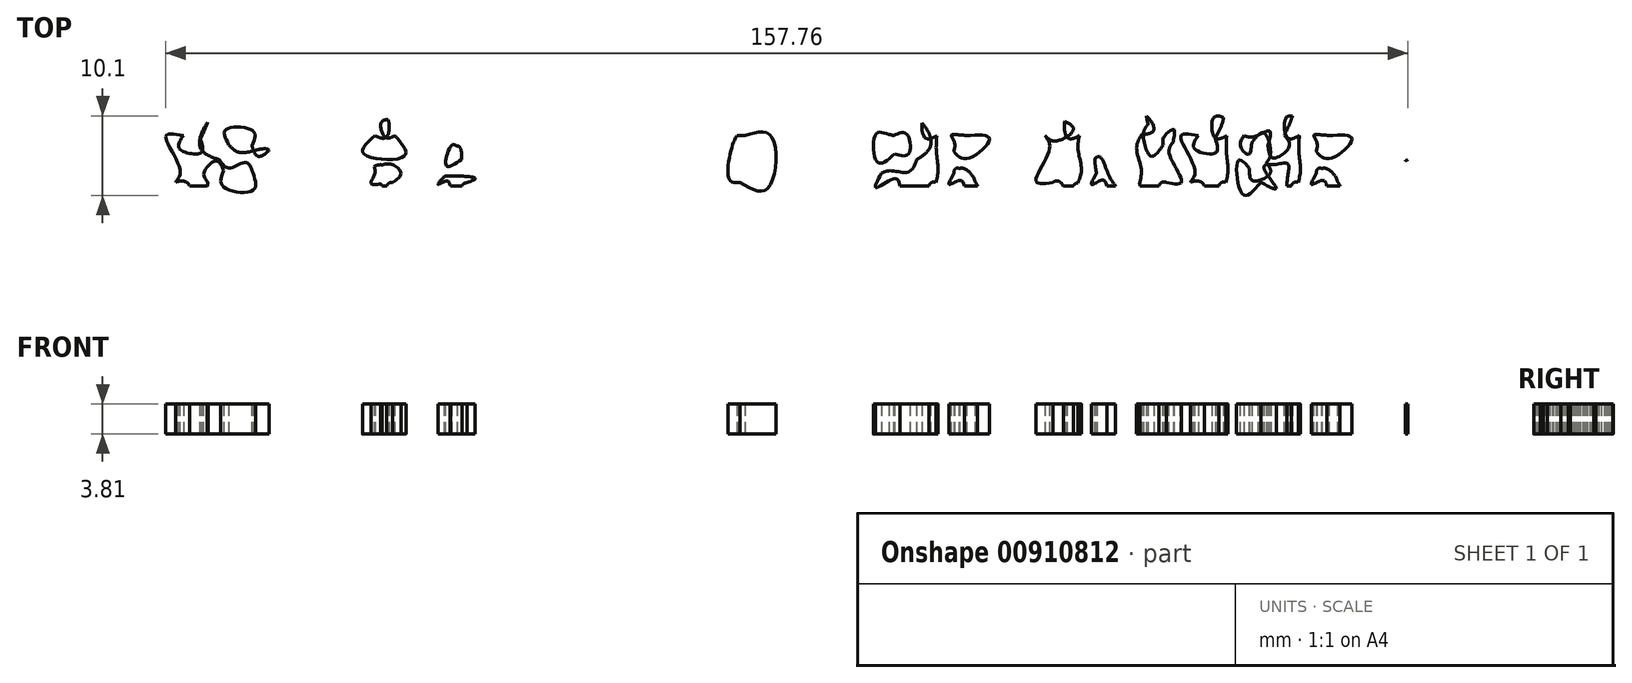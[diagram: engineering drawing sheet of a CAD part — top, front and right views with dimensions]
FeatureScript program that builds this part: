
annotation { "Feature Type Name" : "Feature", "Feature Type Description" : "" }
export const myFeature = defineFeature(function(context is Context, id is Id, definition is map)
    precondition{}
    {
        {
            var Q0;
            Q0=qCreatedBy(makeId("Top.planeOp"),FACE);
            var sketch = newSketch(context, id + "F0", { "sketchPlane" : qUnion([Q0])});
            skLineSegment(sketch, "E0", {"start": v(-392.16, 161.06) * mm, "end": v(-389.78, 161.06) * mm});
            skLineSegment(sketch, "E1", {"start": v(-389.78, 161.06) * mm, "end": v(-385.07, 161.06) * mm});
            skLineSegment(sketch, "E2", {"start": v(-383.48, 161.06) * mm, "end": v(-377.66, 161.06) * mm});
            skLineSegment(sketch, "E3", {"start": v(-374.78, 161.06) * mm, "end": v(-361.4, 161.06) * mm});
            skLineSegment(sketch, "E4", {"start": v(-360.93, 161.06) * mm, "end": v(-360.68, 161.06) * mm});
            skLineSegment(sketch, "E5", {"start": v(-358.96, 161.06) * mm, "end": v(-356.75, 161.06) * mm});
            skLineSegment(sketch, "E6", {"start": v(-356.3, 161.06) * mm, "end": v(-356.04, 161.06) * mm});
            skLineSegment(sketch, "E7", {"start": v(-354.31, 161.06) * mm, "end": v(-352.5, 161.06) * mm});
            skLineSegment(sketch, "E8", {"start": v(-350.4, 161.06) * mm, "end": v(-347.14, 161.06) * mm});
            skLineSegment(sketch, "E9", {"start": v(-346.7, 161.06) * mm, "end": v(-346.26, 161.06) * mm});
            skLineSegment(sketch, "E10", {"start": v(-344.65, 161.06) * mm, "end": v(-341.9, 161.06) * mm});
            skLineSegment(sketch, "E11", {"start": v(-339.56, 161.06) * mm, "end": v(-339.12, 161.06) * mm});
            skLineSegment(sketch, "E12", {"start": v(-336.77, 161.06) * mm, "end": v(-322.47, 161.06) * mm});
            skLineSegment(sketch, "E13", {"start": v(-319.67, 161.06) * mm, "end": v(-315.49, 161.06) * mm});
            skLineSegment(sketch, "E14", {"start": v(-315.06, 161.06) * mm, "end": v(-314.5, 161.06) * mm});
            skLineSegment(sketch, "E15", {"start": v(-311.92, 161.06) * mm, "end": v(-294.7, 161.06) * mm});
            skLineSegment(sketch, "E16", {"start": v(-293.3, 161.06) * mm, "end": v(-286.65, 161.06) * mm});
            skLineSegment(sketch, "E17", {"start": v(-285.25, 161.06) * mm, "end": v(-280.95, 161.06) * mm});
            skLineSegment(sketch, "E18", {"start": v(-280, 161.06) * mm, "end": v(-276.71, 161.06) * mm});
            skLineSegment(sketch, "E19", {"start": v(-274.31, 161.06) * mm, "end": v(-269.46, 161.06) * mm});
            skLineSegment(sketch, "E20", {"start": v(-269.04, 161.06) * mm, "end": v(-268.7, 161.06) * mm});
            skLineSegment(sketch, "E21", {"start": v(-267.03, 161.06) * mm, "end": v(-263.02, 161.06) * mm});
            skLineSegment(sketch, "E22", {"start": v(-262.74, 161.06) * mm, "end": v(-256.16, 161.06) * mm});
            skLineSegment(sketch, "E23", {"start": v(-254.57, 161.06) * mm, "end": v(-240.61, 161.06) * mm});
            skLineSegment(sketch, "E24", {"start": v(-239.21, 161.06) * mm, "end": v(-234.91, 161.06) * mm});
            skLineSegment(sketch, "E25", {"start": v(-233.97, 161.06) * mm, "end": v(-218.67, 161.06) * mm});
            skLineSegment(sketch, "E26", {"start": v(-219.23, 162.84) * mm, "end": v(-224.08, 162.84) * mm});
            skLineSegment(sketch, "E27", {"start": v(-228.3, 162.84) * mm, "end": v(-233.11, 162.84) * mm});
            skLineSegment(sketch, "E28", {"start": v(-242.59, 162.84) * mm, "end": v(-243.12, 162.84) * mm});
            skLineSegment(sketch, "E29", {"start": v(-251.8, 162.84) * mm, "end": v(-253.6, 162.84) * mm});
            skLineSegment(sketch, "E30", {"start": v(-259.4, 162.84) * mm, "end": v(-261.8, 162.84) * mm});
            skLineSegment(sketch, "E31", {"start": v(-270.25, 162.84) * mm, "end": v(-271.55, 162.84) * mm});
            skLineSegment(sketch, "E32", {"start": v(-278.26, 162.84) * mm, "end": v(-279.15, 162.84) * mm});
            skLineSegment(sketch, "E33", {"start": v(-288.63, 162.84) * mm, "end": v(-292.26, 162.84) * mm});
            skLineSegment(sketch, "E34", {"start": v(-297.83, 162.84) * mm, "end": v(-308.5, 162.84) * mm});
            skLineSegment(sketch, "E35", {"start": v(-316.27, 162.84) * mm, "end": v(-317.6, 162.84) * mm});
            skLineSegment(sketch, "E36", {"start": v(-324.8, 162.84) * mm, "end": v(-335.4, 162.84) * mm});
            skLineSegment(sketch, "E37", {"start": v(-343.18, 162.84) * mm, "end": v(-343.57, 162.84) * mm});
            skLineSegment(sketch, "E38", {"start": v(-362.15, 162.84) * mm, "end": v(-372.55, 162.84) * mm});
            skLineSegment(sketch, "E39", {"start": v(-380.27, 162.84) * mm, "end": v(-382.52, 162.84) * mm});
            skLineSegment(sketch, "E40", {"start": v(-388.3, 162.84) * mm, "end": v(-389.78, 162.84) * mm});
            skLineSegment(sketch, "E41", {"start": v(-312.98, 169.2) * mm, "end": v(-311.96, 169.2) * mm});
            skLineSegment(sketch, "E42", {"start": v(-264.94, 162.84) * mm, "end": v(-266, 162.84) * mm});
            skLineSegment(sketch, "E43", {"start": v(-357.5, 162.84) * mm, "end": v(-358.06, 162.84) * mm});
            skLineSegment(sketch, "E44", {"start": v(-282.44, 162.84) * mm, "end": v(-284.08, 162.84) * mm});
            skLineSegment(sketch, "E45", {"start": v(-236.4, 162.84) * mm, "end": v(-238.04, 162.84) * mm});
            skLineSegment(sketch, "E46", {"start": v(-347.92, 162.84) * mm, "end": v(-349.37, 162.84) * mm});
            skFitSpline(sketch, "E47", {"points": [v(-411.77, 178.81) * mm, v(-412, 178.82) * mm, v(-412.23, 178.74) * mm, v(-412.4, 178.59) * mm]});
            skFitSpline(sketch, "E48", {"points": [v(-412.4, 178.59) * mm, v(-412.4, 178.59) * mm, v(-412.4, 178.59) * mm, v(-412.41, 178.58) * mm, v(-414.56, 176.7) * mm, v(-416.6, 174.1) * mm]});
            skFitSpline(sketch, "E49", {"points": [v(-416.6, 174.1) * mm, v(-418.66, 171.49) * mm, v(-420.75, 168.13) * mm, v(-420.28, 164.84) * mm]});
            skFitSpline(sketch, "E50", {"points": [v(-420.28, 164.84) * mm, v(-419.83, 161.73) * mm, v(-417.73, 158.5) * mm, v(-415.02, 155.94) * mm]});
            skFitSpline(sketch, "E51", {"points": [v(-415.02, 155.94) * mm, v(-412.31, 153.37) * mm, v(-408.96, 151.45) * mm, v(-405.73, 151.27) * mm]});
            skFitSpline(sketch, "E52", {"points": [v(-405.73, 151.27) * mm, v(-402.3, 151.08) * mm, v(-398.95, 153.74) * mm, v(-396.34, 156.3) * mm]});
            skFitSpline(sketch, "E53", {"points": [v(-396.34, 156.3) * mm, v(-394.03, 158.55) * mm, v(-392.52, 160.56) * mm, v(-392.16, 161.06) * mm]});
            skFitSpline(sketch, "E54", {"points": [v(-385.07, 161.06) * mm, v(-384.5, 161) * mm, v(-383.96, 160.95) * mm, v(-383.48, 161.06) * mm]});
            skFitSpline(sketch, "E55", {"points": [v(-377.66, 161.06) * mm, v(-376.76, 160.72) * mm, v(-375.7, 160.74) * mm, v(-374.78, 161.06) * mm]});
            skFitSpline(sketch, "E56", {"points": [v(-361.4, 161.06) * mm, v(-361.25, 161.02) * mm, v(-361.1, 161.02) * mm, v(-360.93, 161.06) * mm]});
            skFitSpline(sketch, "E57", {"points": [v(-360.68, 161.06) * mm, v(-360.2, 160.85) * mm, v(-359.53, 160.87) * mm, v(-358.96, 161.06) * mm]});
            skFitSpline(sketch, "E58", {"points": [v(-356.75, 161.06) * mm, v(-356.61, 161.02) * mm, v(-356.46, 161.02) * mm, v(-356.3, 161.06) * mm]});
            skFitSpline(sketch, "E59", {"points": [v(-356.04, 161.06) * mm, v(-355.56, 160.85) * mm, v(-354.89, 160.87) * mm, v(-354.31, 161.06) * mm]});
            skFitSpline(sketch, "E60", {"points": [v(-352.5, 161.06) * mm, v(-351.97, 160.91) * mm, v(-351.12, 160.89) * mm, v(-350.4, 161.06) * mm]});
            skFitSpline(sketch, "E61", {"points": [v(-347.14, 161.06) * mm, v(-347, 161.03) * mm, v(-346.86, 161.02) * mm, v(-346.7, 161.06) * mm]});
            skFitSpline(sketch, "E62", {"points": [v(-346.26, 161.06) * mm, v(-345.8, 161) * mm, v(-345.2, 160.97) * mm, v(-344.65, 161.06) * mm]});
            skFitSpline(sketch, "E63", {"points": [v(-341.9, 161.06) * mm, v(-341.2, 160.9) * mm, v(-340.35, 160.93) * mm, v(-339.56, 161.06) * mm]});
            skFitSpline(sketch, "E64", {"points": [v(-339.12, 161.06) * mm, v(-338.17, 160.89) * mm, v(-337.38, 160.88) * mm, v(-336.77, 161.06) * mm]});
            skFitSpline(sketch, "E65", {"points": [v(-322.47, 161.06) * mm, v(-321.92, 160.93) * mm, v(-321.35, 160.87) * mm, v(-320.9, 160.86) * mm]});
            skFitSpline(sketch, "E66", {"points": [v(-320.9, 160.86) * mm, v(-320.48, 160.84) * mm, v(-320.06, 160.91) * mm, v(-319.67, 161.06) * mm]});
            skFitSpline(sketch, "E67", {"points": [v(-315.49, 161.06) * mm, v(-315.35, 161.03) * mm, v(-315.21, 161.03) * mm, v(-315.06, 161.06) * mm]});
            skFitSpline(sketch, "E68", {"points": [v(-314.5, 161.06) * mm, v(-313.67, 160.97) * mm, v(-312.78, 160.95) * mm, v(-311.92, 161.06) * mm]});
            skFitSpline(sketch, "E69", {"points": [v(-294.7, 161.06) * mm, v(-294.2, 161) * mm, v(-293.72, 160.98) * mm, v(-293.3, 161.06) * mm]});
            skFitSpline(sketch, "E70", {"points": [v(-286.65, 161.06) * mm, v(-286.2, 161.03) * mm, v(-285.7, 161) * mm, v(-285.25, 161.06) * mm]});
            skFitSpline(sketch, "E71", {"points": [v(-280.95, 161.06) * mm, v(-280.69, 160.96) * mm, v(-280.38, 160.95) * mm, v(-280, 161.06) * mm]});
            skFitSpline(sketch, "E72", {"points": [v(-276.71, 161.06) * mm, v(-275.93, 160.98) * mm, v(-275.12, 161) * mm, v(-274.31, 161.06) * mm]});
            skFitSpline(sketch, "E73", {"points": [v(-269.46, 161.06) * mm, v(-269.33, 161.03) * mm, v(-269.19, 161.03) * mm, v(-269.04, 161.06) * mm]});
            skFitSpline(sketch, "E74", {"points": [v(-268.7, 161.06) * mm, v(-268.25, 160.96) * mm, v(-267.6, 160.94) * mm, v(-267.03, 161.06) * mm]});
            skFitSpline(sketch, "E75", {"points": [v(-263.02, 161.06) * mm, v(-262.93, 161.05) * mm, v(-262.83, 161.05) * mm, v(-262.74, 161.06) * mm]});
            skFitSpline(sketch, "E76", {"points": [v(-256.16, 161.06) * mm, v(-255.6, 161) * mm, v(-255.05, 160.95) * mm, v(-254.57, 161.06) * mm]});
            skFitSpline(sketch, "E77", {"points": [v(-240.61, 161.06) * mm, v(-240.16, 161.03) * mm, v(-239.66, 161) * mm, v(-239.21, 161.06) * mm]});
            skFitSpline(sketch, "E78", {"points": [v(-234.91, 161.06) * mm, v(-234.65, 160.96) * mm, v(-234.34, 160.95) * mm, v(-233.97, 161.06) * mm]});
            skFitSpline(sketch, "E79", {"points": [v(-218.67, 161.06) * mm, v(-218.3, 161.05) * mm, v(-217.97, 161.28) * mm, v(-217.84, 161.63) * mm]});
            skFitSpline(sketch, "E80", {"points": [v(-217.84, 161.63) * mm, v(-217.4, 161.82) * mm, v(-217.05, 162.25) * mm, v(-217.08, 162.82) * mm]});
            skFitSpline(sketch, "E81", {"points": [v(-217.08, 162.82) * mm, v(-215.9, 167) * mm, v(-218.01, 171.83) * mm, v(-221.91, 173.63) * mm]});
            skFitSpline(sketch, "E82", {"points": [v(-221.91, 173.63) * mm, v(-222.1, 173.67) * mm, v(-222.3, 173.64) * mm, v(-222.47, 173.56) * mm]});
            skFitSpline(sketch, "E83", {"points": [v(-222.47, 173.56) * mm, v(-224.14, 172.5) * mm, v(-222, 171.05) * mm, v(-221.2, 170.27) * mm]});
            skFitSpline(sketch, "E84", {"points": [v(-221.2, 170.27) * mm, v(-219.3, 168.29) * mm, v(-218.98, 165.47) * mm, v(-219.23, 162.84) * mm]});
            skFitSpline(sketch, "E85", {"points": [v(-224.08, 162.84) * mm, v(-223.18, 164.27) * mm, v(-223.73, 166.65) * mm, v(-225.8, 166.73) * mm]});
            skFitSpline(sketch, "E86", {"points": [v(-225.8, 166.73) * mm, v(-225.9, 166.74) * mm, v(-226.01, 166.74) * mm, v(-226.11, 166.74) * mm]});
            skFitSpline(sketch, "E87", {"points": [v(-227.8, 166.15) * mm, v(-228.88, 165.4) * mm, v(-228.92, 163.9) * mm, v(-228.3, 162.84) * mm]});
            skFitSpline(sketch, "E88", {"points": [v(-233.11, 162.84) * mm, v(-233.31, 163.15) * mm, v(-233.65, 163.36) * mm, v(-234.1, 163.28) * mm]});
            skFitSpline(sketch, "E89", {"points": [v(-234.1, 163.28) * mm, v(-234.42, 164.16) * mm, v(-235.54, 165.19) * mm, v(-235.61, 165.85) * mm]});
            skFitSpline(sketch, "E90", {"points": [v(-235.61, 165.85) * mm, v(-233.22, 167.2) * mm, v(-234.4, 170.84) * mm, v(-236.83, 171.27) * mm]});
            skFitSpline(sketch, "E91", {"points": [v(-236.83, 171.27) * mm, v(-238.4, 171.6) * mm, v(-240.06, 171.3) * mm, v(-241.66, 171.4) * mm]});
            skFitSpline(sketch, "E92", {"points": [v(-241.66, 171.4) * mm, v(-243.21, 171.52) * mm, v(-243.08, 168.97) * mm, v(-241.56, 169.2) * mm]});
            skFitSpline(sketch, "E93", {"points": [v(-241.56, 169.2) * mm, v(-241.63, 167.27) * mm, v(-241.42, 165.05) * mm, v(-241.66, 163.28) * mm]});
            skFitSpline(sketch, "E94", {"points": [v(-241.66, 163.28) * mm, v(-242.1, 163.32) * mm, v(-242.41, 163.13) * mm, v(-242.59, 162.84) * mm]});
            skFitSpline(sketch, "E95", {"points": [v(-243.12, 162.84) * mm, v(-243.02, 164.19) * mm, v(-243, 165.62) * mm, v(-244.52, 165.51) * mm]});
            skFitSpline(sketch, "E96", {"points": [v(-244.52, 165.51) * mm, v(-246.05, 165.2) * mm, v(-244.5, 162.54) * mm, v(-246.47, 163.28) * mm]});
            skFitSpline(sketch, "E97", {"points": [v(-246.47, 163.28) * mm, v(-248.75, 161.76) * mm, v(-249.32, 166.02) * mm, v(-247.87, 165.01) * mm]});
            skFitSpline(sketch, "E98", {"points": [v(-247.87, 165.01) * mm, v(-247.47, 163.5) * mm, v(-245.28, 164.38) * mm, v(-245.75, 165.79) * mm]});
            skFitSpline(sketch, "E99", {"points": [v(-245.75, 165.79) * mm, v(-245.2, 166.97) * mm, v(-246.08, 169.56) * mm, v(-247.6, 168.3) * mm]});
            skFitSpline(sketch, "E100", {"points": [v(-247.6, 168.3) * mm, v(-248.03, 166.83) * mm, v(-249.02, 167.86) * mm, v(-248.6, 169.2) * mm]});
            skFitSpline(sketch, "E101", {"points": [v(-248.6, 169.2) * mm, v(-247.22, 169.1) * mm, v(-245.35, 169.8) * mm, v(-245.55, 167.96) * mm]});
            skFitSpline(sketch, "E102", {"points": [v(-245.55, 167.96) * mm, v(-244.86, 166.37) * mm, v(-242.84, 167.85) * mm, v(-243.47, 169.24) * mm]});
            skFitSpline(sketch, "E103", {"points": [v(-243.47, 169.24) * mm, v(-242.5, 172.63) * mm, v(-246.43, 171.06) * mm, v(-248.46, 171.4) * mm]});
            skFitSpline(sketch, "E104", {"points": [v(-248.46, 171.4) * mm, v(-249.27, 171.4) * mm, v(-250.07, 171.4) * mm, v(-250.87, 171.4) * mm]});
            skFitSpline(sketch, "E105", {"points": [v(-250.87, 171.4) * mm, v(-252.42, 171.52) * mm, v(-252.29, 168.97) * mm, v(-250.77, 169.2) * mm]});
            skFitSpline(sketch, "E106", {"points": [v(-250.77, 169.2) * mm, v(-250.84, 167.27) * mm, v(-250.63, 165.05) * mm, v(-250.86, 163.28) * mm]});
            skFitSpline(sketch, "E107", {"points": [v(-250.86, 163.28) * mm, v(-251.31, 163.32) * mm, v(-251.62, 163.13) * mm, v(-251.8, 162.84) * mm]});
            skFitSpline(sketch, "E108", {"points": [v(-253.6, 162.84) * mm, v(-254, 163.3) * mm, v(-254.83, 163.43) * mm, v(-255.41, 163.28) * mm]});
            skFitSpline(sketch, "E109", {"points": [v(-255.41, 163.28) * mm, v(-254.85, 165.03) * mm, v(-256.62, 169.14) * mm, v(-254.4, 169.2) * mm]});
            skFitSpline(sketch, "E110", {"points": [v(-254.4, 169.2) * mm, v(-254.89, 167.58) * mm, v(-252.19, 167.03) * mm, v(-252.24, 168.8) * mm]});
            skFitSpline(sketch, "E111", {"points": [v(-252.24, 168.8) * mm, v(-251.32, 171.9) * mm, v(-253.82, 171.53) * mm, v(-256.07, 171.4) * mm]});
            skFitSpline(sketch, "E112", {"points": [v(-256.07, 171.4) * mm, v(-257.39, 171) * mm, v(-260.75, 172.27) * mm, v(-260.77, 170.62) * mm]});
            skFitSpline(sketch, "E113", {"points": [v(-260.77, 170.62) * mm, v(-261.37, 169.39) * mm, v(-260.4, 166.61) * mm, v(-258.85, 168.05) * mm]});
            skFitSpline(sketch, "E114", {"points": [v(-258.85, 168.05) * mm, v(-258.75, 169.07) * mm, v(-257.54, 169.97) * mm, v(-257.58, 168.43) * mm]});
            skFitSpline(sketch, "E115", {"points": [v(-257.58, 168.43) * mm, v(-258.08, 166.92) * mm, v(-256.52, 163.33) * mm, v(-258.46, 163.28) * mm]});
            skFitSpline(sketch, "E116", {"points": [v(-258.46, 163.28) * mm, v(-258.9, 163.32) * mm, v(-259.21, 163.13) * mm, v(-259.4, 162.84) * mm]});
            skFitSpline(sketch, "E117", {"points": [v(-261.8, 162.84) * mm, v(-261.82, 162.9) * mm, v(-261.84, 162.97) * mm, v(-261.86, 163.03) * mm]});
            skFitSpline(sketch, "E118", {"points": [v(-261.86, 163.03) * mm, v(-261.66, 165.04) * mm, v(-262.24, 167.64) * mm, v(-261.6, 169.3) * mm]});
            skFitSpline(sketch, "E119", {"points": [v(-261.6, 169.3) * mm, v(-260.04, 170.02) * mm, v(-261.5, 172.03) * mm, v(-262.87, 171.4) * mm]});
            skFitSpline(sketch, "E120", {"points": [v(-262.87, 171.4) * mm, v(-264.14, 172.1) * mm, v(-266.66, 170.74) * mm, v(-265.1, 169.4) * mm]});
            skFitSpline(sketch, "E121", {"points": [v(-265.1, 169.4) * mm, v(-263.7, 169.28) * mm, v(-264, 168.17) * mm, v(-264.02, 166.87) * mm]});
            skFitSpline(sketch, "E122", {"points": [v(-264.02, 166.87) * mm, v(-263.87, 163.95) * mm, v(-266.1, 169.65) * mm, v(-267, 170.56) * mm]});
            skFitSpline(sketch, "E123", {"points": [v(-267, 170.56) * mm, v(-267.36, 171.93) * mm, v(-268.58, 171.23) * mm, v(-269.6, 171.4) * mm]});
            skFitSpline(sketch, "E124", {"points": [v(-269.6, 171.4) * mm, v(-271.16, 171.52) * mm, v(-271.03, 168.97) * mm, v(-269.5, 169.2) * mm]});
            skFitSpline(sketch, "E125", {"points": [v(-269.5, 169.2) * mm, v(-269.65, 167.28) * mm, v(-269.24, 164.9) * mm, v(-269.69, 163.22) * mm]});
            skFitSpline(sketch, "E126", {"points": [v(-269.69, 163.22) * mm, v(-269.95, 163.14) * mm, v(-270.13, 163) * mm, v(-270.25, 162.84) * mm]});
            skFitSpline(sketch, "E127", {"points": [v(-271.55, 162.84) * mm, v(-271.84, 163.23) * mm, v(-272.32, 163.47) * mm, v(-272.86, 163.28) * mm]});
            skFitSpline(sketch, "E128", {"points": [v(-272.86, 163.28) * mm, v(-274.99, 163.44) * mm, v(-273.31, 167.44) * mm, v(-273.85, 169.2) * mm]});
            skFitSpline(sketch, "E129", {"points": [v(-273.85, 169.2) * mm, v(-272.57, 168.52) * mm, v(-270.25, 169.98) * mm, v(-271.78, 171.22) * mm]});
            skFitSpline(sketch, "E130", {"points": [v(-271.78, 171.22) * mm, v(-273.54, 171.74) * mm, v(-275.6, 171.2) * mm, v(-277.42, 171.4) * mm]});
            skFitSpline(sketch, "E131", {"points": [v(-277.42, 171.4) * mm, v(-278.92, 171.52) * mm, v(-278.87, 169.03) * mm, v(-277.38, 169.2) * mm]});
            skFitSpline(sketch, "E132", {"points": [v(-277.38, 169.2) * mm, v(-274.64, 169.57) * mm, v(-276.6, 165.18) * mm, v(-276.01, 163.38) * mm]});
            skFitSpline(sketch, "E133", {"points": [v(-276.01, 163.38) * mm, v(-276.62, 163.63) * mm, v(-277.72, 163.38) * mm, v(-278.26, 162.84) * mm]});
            skFitSpline(sketch, "E134", {"points": [v(-279.15, 162.84) * mm, v(-279.35, 163.15) * mm, v(-279.69, 163.36) * mm, v(-280.14, 163.28) * mm]});
            skFitSpline(sketch, "E135", {"points": [v(-280.14, 163.28) * mm, v(-280.46, 164.16) * mm, v(-281.58, 165.19) * mm, v(-281.65, 165.85) * mm]});
            skFitSpline(sketch, "E136", {"points": [v(-281.65, 165.85) * mm, v(-279.26, 167.2) * mm, v(-280.44, 170.84) * mm, v(-282.87, 171.27) * mm]});
            skFitSpline(sketch, "E137", {"points": [v(-282.87, 171.27) * mm, v(-284.45, 171.6) * mm, v(-286.1, 171.3) * mm, v(-287.7, 171.4) * mm]});
            skFitSpline(sketch, "E138", {"points": [v(-287.7, 171.4) * mm, v(-289.25, 171.52) * mm, v(-289.12, 168.97) * mm, v(-287.6, 169.2) * mm]});
            skFitSpline(sketch, "E139", {"points": [v(-287.6, 169.2) * mm, v(-287.67, 167.27) * mm, v(-287.46, 165.05) * mm, v(-287.7, 163.28) * mm]});
            skFitSpline(sketch, "E140", {"points": [v(-287.7, 163.28) * mm, v(-288.14, 163.32) * mm, v(-288.45, 163.13) * mm, v(-288.63, 162.84) * mm]});
            skFitSpline(sketch, "E141", {"points": [v(-292.26, 162.84) * mm, v(-292.94, 163.76) * mm, v(-295.33, 162.6) * mm, v(-294.64, 164.45) * mm]});
            skFitSpline(sketch, "E142", {"points": [v(-294.64, 164.45) * mm, v(-293.43, 164.75) * mm, v(-291.2, 164.61) * mm, v(-290.18, 166.13) * mm]});
            skFitSpline(sketch, "E143", {"points": [v(-290.18, 166.13) * mm, v(-288.33, 168.3) * mm, v(-290.55, 171.66) * mm, v(-293.18, 171.4) * mm]});
            skFitSpline(sketch, "E144", {"points": [v(-293.18, 171.4) * mm, v(-294.43, 171.4) * mm, v(-295.67, 171.4) * mm, v(-296.9, 171.4) * mm]});
            skFitSpline(sketch, "E145", {"points": [v(-296.9, 171.4) * mm, v(-298.46, 171.52) * mm, v(-298.33, 168.97) * mm, v(-296.8, 169.2) * mm]});
            skFitSpline(sketch, "E146", {"points": [v(-296.8, 169.2) * mm, v(-296.88, 167.27) * mm, v(-296.67, 165.05) * mm, v(-296.9, 163.28) * mm]});
            skFitSpline(sketch, "E147", {"points": [v(-296.9, 163.28) * mm, v(-297.35, 163.32) * mm, v(-297.66, 163.13) * mm, v(-297.83, 162.84) * mm]});
            skFitSpline(sketch, "E148", {"points": [v(-308.5, 162.84) * mm, v(-308.34, 163.07) * mm, v(-308.2, 163.33) * mm, v(-308.08, 163.62) * mm]});
            skFitSpline(sketch, "E149", {"points": [v(-308.08, 163.62) * mm, v(-306.73, 166.5) * mm, v(-307.93, 171.03) * mm, v(-311.48, 171.38) * mm]});
            skFitSpline(sketch, "E150", {"points": [v(-311.48, 171.38) * mm, v(-312.76, 171.44) * mm, v(-314.05, 171.38) * mm, v(-315.33, 171.4) * mm]});
            skFitSpline(sketch, "E151", {"points": [v(-315.33, 171.4) * mm, v(-316.66, 171.54) * mm, v(-316.88, 169.33) * mm, v(-315.53, 169.23) * mm]});
            skFitSpline(sketch, "E152", {"points": [v(-315.53, 169.23) * mm, v(-315.67, 167.3) * mm, v(-315.26, 164.9) * mm, v(-315.71, 163.22) * mm]});
            skFitSpline(sketch, "E153", {"points": [v(-315.71, 163.22) * mm, v(-315.97, 163.14) * mm, v(-316.15, 163) * mm, v(-316.27, 162.84) * mm]});
            skFitSpline(sketch, "E154", {"points": [v(-317.6, 162.84) * mm, v(-316.94, 164.03) * mm, v(-316.9, 165.52) * mm, v(-317.99, 166.63) * mm]});
            skFitSpline(sketch, "E155", {"points": [v(-317.99, 166.63) * mm, v(-318.84, 167.19) * mm, v(-317.18, 167.94) * mm, v(-317.48, 168.85) * mm]});
            skFitSpline(sketch, "E156", {"points": [v(-317.48, 168.85) * mm, v(-317.28, 170.87) * mm, v(-319.27, 172.43) * mm, v(-321.16, 172.25) * mm]});
            skFitSpline(sketch, "E157", {"points": [v(-321.16, 172.25) * mm, v(-322.52, 172.2) * mm, v(-325.04, 171.13) * mm, v(-324.19, 169.41) * mm]});
            skFitSpline(sketch, "E158", {"points": [v(-324.19, 169.41) * mm, v(-322.8, 168) * mm, v(-321.53, 171.3) * mm, v(-319.96, 169.73) * mm]});
            skFitSpline(sketch, "E159", {"points": [v(-319.96, 169.73) * mm, v(-318.85, 168.44) * mm, v(-320.82, 168.01) * mm, v(-321.78, 168.05) * mm]});
            skFitSpline(sketch, "E160", {"points": [v(-321.78, 168.05) * mm, v(-323.18, 167.49) * mm, v(-322.17, 165.53) * mm, v(-320.87, 165.91) * mm]});
            skFitSpline(sketch, "E161", {"points": [v(-320.87, 165.91) * mm, v(-318.84, 165.91) * mm, v(-318.88, 162.98) * mm, v(-320.9, 163.06) * mm]});
            skFitSpline(sketch, "E162", {"points": [v(-320.9, 163.06) * mm, v(-322.28, 162.68) * mm, v(-323.93, 165.12) * mm, v(-324.81, 163.24) * mm]});
            skFitSpline(sketch, "E163", {"points": [v(-324.81, 163.24) * mm, v(-324.82, 163.1) * mm, v(-324.81, 162.97) * mm, v(-324.8, 162.84) * mm]});
            skFitSpline(sketch, "E164", {"points": [v(-335.4, 162.84) * mm, v(-335.36, 163.33) * mm, v(-335.42, 163.9) * mm, v(-335.58, 164.59) * mm]});
            skFitSpline(sketch, "E165", {"points": [v(-335.58, 164.59) * mm, v(-335.3, 166.18) * mm, v(-337.9, 166.32) * mm, v(-337.75, 164.7) * mm]});
            skFitSpline(sketch, "E166", {"points": [v(-337.75, 164.7) * mm, v(-337.82, 161.65) * mm, v(-342.05, 163.67) * mm, v(-338.57, 165.81) * mm]});
            skFitSpline(sketch, "E167", {"points": [v(-338.57, 165.81) * mm, v(-337.62, 167.44) * mm, v(-334.9, 169.83) * mm, v(-336.38, 171.4) * mm]});
            skFitSpline(sketch, "E168", {"points": [v(-336.38, 171.4) * mm, v(-338.23, 170.93) * mm, v(-342.36, 172.37) * mm, v(-342.9, 170.62) * mm]});
            skFitSpline(sketch, "E169", {"points": [v(-342.9, 170.62) * mm, v(-342.89, 169.5) * mm, v(-343.45, 166.57) * mm, v(-341.43, 167) * mm]});
            skFitSpline(sketch, "E170", {"points": [v(-341.43, 167) * mm, v(-340.03, 167.44) * mm, v(-341.53, 169.93) * mm, v(-339.58, 169.2) * mm]});
            skFitSpline(sketch, "E171", {"points": [v(-339.58, 169.2) * mm, v(-338.33, 168.59) * mm, v(-341.9, 165.46) * mm, v(-342.61, 163.83) * mm]});
            skFitSpline(sketch, "E172", {"points": [v(-342.61, 163.83) * mm, v(-342.9, 163.46) * mm, v(-343.07, 163.13) * mm, v(-343.18, 162.84) * mm]});
            skFitSpline(sketch, "E173", {"points": [v(-343.57, 162.84) * mm, v(-344.08, 163.43) * mm, v(-345.11, 163.14) * mm, v(-344.97, 164.37) * mm]});
            skFitSpline(sketch, "E174", {"points": [v(-344.97, 164.37) * mm, v(-345.85, 166.72) * mm, v(-346.72, 169.06) * mm, v(-347.6, 171.4) * mm]});
            skFitSpline(sketch, "E175", {"points": [v(-347.6, 171.4) * mm, v(-348.83, 171.4) * mm, v(-350.06, 171.4) * mm, v(-351.3, 171.4) * mm]});
            skFitSpline(sketch, "E176", {"points": [v(-351.3, 171.4) * mm, v(-352.8, 171.52) * mm, v(-352.75, 169.03) * mm, v(-351.26, 169.2) * mm]});
            skFitSpline(sketch, "E177", {"points": [v(-351.26, 169.2) * mm, v(-349.85, 168.56) * mm, v(-352.47, 165.08) * mm, v(-352.7, 163.28) * mm]});
            skFitSpline(sketch, "E178", {"points": [v(-352.7, 163.28) * mm, v(-353.06, 163.3) * mm, v(-353.33, 163.18) * mm, v(-353.51, 162.98) * mm]});
            skFitSpline(sketch, "E179", {"points": [v(-353.51, 162.98) * mm, v(-353.53, 163) * mm, v(-353.55, 163.03) * mm, v(-353.58, 163.06) * mm]});
            skFitSpline(sketch, "E180", {"points": [v(-353.58, 163.06) * mm, v(-355.2, 163.45) * mm, v(-353.85, 165.9) * mm, v(-354.3, 167.17) * mm]});
            skFitSpline(sketch, "E181", {"points": [v(-354.3, 167.17) * mm, v(-354.44, 168.37) * mm, v(-354.4, 169.21) * mm, v(-353.55, 169.95) * mm]});
            skFitSpline(sketch, "E182", {"points": [v(-353.55, 169.95) * mm, v(-353.2, 171.9) * mm, v(-355.92, 171.55) * mm, v(-357.09, 171.29) * mm]});
            skFitSpline(sketch, "E183", {"points": [v(-357.09, 171.29) * mm, v(-358.21, 170.81) * mm, v(-357.63, 169) * mm, v(-356.46, 169.2) * mm]});
            skFitSpline(sketch, "E184", {"points": [v(-356.46, 169.2) * mm, v(-355.24, 166.6) * mm, v(-360.4, 166.92) * mm, v(-358.98, 169.2) * mm]});
            skFitSpline(sketch, "E185", {"points": [v(-358.98, 169.2) * mm, v(-357.47, 169.06) * mm, v(-357.5, 171.57) * mm, v(-359, 171.4) * mm]});
            skFitSpline(sketch, "E186", {"points": [v(-359, 171.4) * mm, v(-359.63, 171.4) * mm, v(-360.26, 171.4) * mm, v(-360.89, 171.4) * mm]});
            skFitSpline(sketch, "E187", {"points": [v(-360.89, 171.4) * mm, v(-362.14, 171.53) * mm, v(-362.47, 169.51) * mm, v(-361.23, 169.25) * mm]});
            skFitSpline(sketch, "E188", {"points": [v(-361.23, 169.25) * mm, v(-361.35, 167.32) * mm, v(-361, 164.95) * mm, v(-361.39, 163.27) * mm]});
            skFitSpline(sketch, "E189", {"points": [v(-361.39, 163.27) * mm, v(-361.76, 163.22) * mm, v(-362, 163.06) * mm, v(-362.15, 162.84) * mm]});
            skFitSpline(sketch, "E190", {"points": [v(-372.55, 162.84) * mm, v(-372.27, 163.4) * mm, v(-372.15, 164.05) * mm, v(-372.28, 164.79) * mm]});
            skFitSpline(sketch, "E191", {"points": [v(-372.28, 164.79) * mm, v(-372.55, 167.47) * mm, v(-375.87, 167.05) * mm, v(-377.54, 168.05) * mm]});
            skFitSpline(sketch, "E192", {"points": [v(-377.54, 168.05) * mm, v(-377.93, 169.95) * mm, v(-374.44, 169.79) * mm, v(-374.6, 167.95) * mm]});
            skFitSpline(sketch, "E193", {"points": [v(-374.6, 167.95) * mm, v(-373.74, 166.57) * mm, v(-372.02, 168.08) * mm, v(-372.58, 169.38) * mm]});
            skFitSpline(sketch, "E194", {"points": [v(-372.58, 169.38) * mm, v(-372.16, 170.52) * mm, v(-373.27, 172.01) * mm, v(-374.39, 171.16) * mm]});
            skFitSpline(sketch, "E195", {"points": [v(-374.39, 171.16) * mm, v(-374.96, 171.47) * mm, v(-375.6, 171.6) * mm, v(-376.25, 171.6) * mm]});
            skFitSpline(sketch, "E196", {"points": [v(-376.25, 171.6) * mm, v(-379.07, 171.99) * mm, v(-381.22, 167.91) * mm, v(-378.72, 166.14) * mm]});
            skFitSpline(sketch, "E197", {"points": [v(-378.72, 166.14) * mm, v(-377.53, 165.1) * mm, v(-375.37, 165.78) * mm, v(-374.48, 164.47) * mm]});
            skFitSpline(sketch, "E198", {"points": [v(-374.48, 164.47) * mm, v(-374.45, 162.3) * mm, v(-378.27, 162.73) * mm, v(-378.21, 164.78) * mm]});
            skFitSpline(sketch, "E199", {"points": [v(-378.21, 164.78) * mm, v(-379.16, 166) * mm, v(-380.7, 164.48) * mm, v(-380.17, 163.25) * mm]});
            skFitSpline(sketch, "E200", {"points": [v(-380.17, 163.25) * mm, v(-380.22, 163.12) * mm, v(-380.25, 162.98) * mm, v(-380.27, 162.84) * mm]});
            skFitSpline(sketch, "E201", {"points": [v(-382.52, 162.84) * mm, v(-382.91, 163.3) * mm, v(-383.74, 163.43) * mm, v(-384.33, 163.28) * mm]});
            skFitSpline(sketch, "E202", {"points": [v(-384.33, 163.28) * mm, v(-383.76, 165.03) * mm, v(-385.53, 169.14) * mm, v(-383.31, 169.2) * mm]});
            skFitSpline(sketch, "E203", {"points": [v(-383.31, 169.2) * mm, v(-383.8, 167.58) * mm, v(-381.1, 167.03) * mm, v(-381.15, 168.8) * mm]});
            skFitSpline(sketch, "E204", {"points": [v(-381.15, 168.8) * mm, v(-380.23, 171.9) * mm, v(-382.73, 171.53) * mm, v(-384.99, 171.4) * mm]});
            skFitSpline(sketch, "E205", {"points": [v(-384.99, 171.4) * mm, v(-386.3, 171) * mm, v(-389.66, 172.27) * mm, v(-389.68, 170.62) * mm]});
            skFitSpline(sketch, "E206", {"points": [v(-389.68, 170.62) * mm, v(-390.28, 169.39) * mm, v(-389.31, 166.61) * mm, v(-387.76, 168.05) * mm]});
            skFitSpline(sketch, "E207", {"points": [v(-387.76, 168.05) * mm, v(-387.67, 169.07) * mm, v(-386.45, 169.97) * mm, v(-386.5, 168.43) * mm]});
            skFitSpline(sketch, "E208", {"points": [v(-386.5, 168.43) * mm, v(-387, 166.92) * mm, v(-385.43, 163.33) * mm, v(-387.37, 163.28) * mm]});
            skFitSpline(sketch, "E209", {"points": [v(-387.37, 163.28) * mm, v(-387.82, 163.32) * mm, v(-388.13, 163.13) * mm, v(-388.3, 162.84) * mm]});
            skFitSpline(sketch, "E210", {"points": [v(-389.78, 162.84) * mm, v(-389.78, 162.84) * mm, v(-389.78, 162.84) * mm, v(-389.8, 162.84) * mm, v(-392.57, 162.84) * mm, v(-392.59, 162.84) * mm, v(-392.59, 162.84) * mm, v(-392.59, 162.84) * mm]});
            skFitSpline(sketch, "E211", {"points": [v(-392.59, 162.84) * mm, v(-392.87, 162.84) * mm, v(-393.14, 162.7) * mm, v(-393.3, 162.48) * mm]});
            skFitSpline(sketch, "E212", {"points": [v(-393.3, 162.48) * mm, v(-393.3, 162.48) * mm, v(-393.3, 162.48) * mm, v(-393.3, 162.47) * mm, v(-395.09, 160) * mm, v(-397.57, 157.58) * mm]});
            skFitSpline(sketch, "E213", {"points": [v(-397.57, 157.58) * mm, v(-400.05, 155.16) * mm, v(-403.25, 152.93) * mm, v(-405.63, 153.06) * mm]});
            skFitSpline(sketch, "E214", {"points": [v(-405.63, 153.06) * mm, v(-408.22, 153.2) * mm, v(-411.32, 154.88) * mm, v(-413.82, 157.24) * mm]});
            skFitSpline(sketch, "E215", {"points": [v(-413.82, 157.24) * mm, v(-416.3, 159.6) * mm, v(-418.17, 162.62) * mm, v(-418.53, 165.1) * mm]});
            skFitSpline(sketch, "E216", {"points": [v(-418.53, 165.1) * mm, v(-418.86, 167.4) * mm, v(-417.16, 170.52) * mm, v(-415.23, 172.98) * mm]});
            skFitSpline(sketch, "E217", {"points": [v(-415.23, 172.98) * mm, v(-413.3, 175.43) * mm, v(-411.26, 177.22) * mm, v(-411.24, 177.23) * mm, v(-411.24, 177.23) * mm, v(-411.24, 177.23) * mm]});
            skFitSpline(sketch, "E218", {"points": [v(-411.24, 177.23) * mm, v(-410.97, 177.47) * mm, v(-410.86, 177.86) * mm, v(-410.98, 178.2) * mm]});
            skFitSpline(sketch, "E219", {"points": [v(-410.98, 178.2) * mm, v(-411.1, 178.56) * mm, v(-411.41, 178.8) * mm, v(-411.77, 178.81) * mm]});
            skFitSpline(sketch, "E220", {"points": [v(-226.11, 166.74) * mm, v(-224.62, 168) * mm, v(-225, 171.09) * mm, v(-227.38, 171.19) * mm]});
            skFitSpline(sketch, "E221", {"points": [v(-227.38, 171.19) * mm, v(-227.88, 171.24) * mm, v(-228.38, 171.1) * mm, v(-228.83, 170.88) * mm]});
            skFitSpline(sketch, "E222", {"points": [v(-228.83, 170.88) * mm, v(-231.38, 169.95) * mm, v(-230.26, 165.91) * mm, v(-227.8, 166.15) * mm]});
            skFitSpline(sketch, "E223", {"points": [v(-293.7, 169.34) * mm, v(-293.54, 169.34) * mm, v(-293.34, 169.3) * mm, v(-293.13, 169.2) * mm]});
            skFitSpline(sketch, "E224", {"points": [v(-293.13, 169.2) * mm, v(-291.45, 169.41) * mm, v(-291.19, 166.9) * mm, v(-292.98, 166.9) * mm]});
            skFitSpline(sketch, "E225", {"points": [v(-292.98, 166.9) * mm, v(-295.13, 165.84) * mm, v(-295.36, 169.38) * mm, v(-293.7, 169.34) * mm]});
            skFitSpline(sketch, "E226", {"points": [v(-284.78, 169.3) * mm, v(-284.55, 169.31) * mm, v(-284.25, 169.28) * mm, v(-283.86, 169.2) * mm]});
            skFitSpline(sketch, "E227", {"points": [v(-283.86, 169.2) * mm, v(-280.91, 168.8) * mm, v(-283.71, 166.3) * mm, v(-285.43, 167.19) * mm]});
            skFitSpline(sketch, "E228", {"points": [v(-285.43, 167.19) * mm, v(-285.4, 168.47) * mm, v(-285.76, 169.26) * mm, v(-284.78, 169.3) * mm]});
            skFitSpline(sketch, "E229", {"points": [v(-238.74, 169.3) * mm, v(-238.51, 169.31) * mm, v(-238.21, 169.28) * mm, v(-237.82, 169.2) * mm]});
            skFitSpline(sketch, "E230", {"points": [v(-237.82, 169.2) * mm, v(-234.87, 168.8) * mm, v(-237.67, 166.3) * mm, v(-239.4, 167.19) * mm]});
            skFitSpline(sketch, "E231", {"points": [v(-239.4, 167.19) * mm, v(-239.36, 168.47) * mm, v(-239.72, 169.26) * mm, v(-238.74, 169.3) * mm]});
            skFitSpline(sketch, "E232", {"points": [v(-311.96, 169.2) * mm, v(-308.61, 169.11) * mm, v(-309.09, 162.51) * mm, v(-312.62, 163.28) * mm]});
            skFitSpline(sketch, "E233", {"points": [v(-312.62, 163.28) * mm, v(-314, 163.69) * mm, v(-313.48, 168.22) * mm, v(-312.98, 169.2) * mm]});
            skFitSpline(sketch, "E234", {"points": [v(-348.56, 167.9) * mm, v(-348.3, 167.86) * mm, v(-348.05, 167.41) * mm, v(-347.96, 166.2) * mm]});
            skFitSpline(sketch, "E235", {"points": [v(-347.96, 166.2) * mm, v(-349.92, 165.45) * mm, v(-349.22, 168) * mm, v(-348.56, 167.9) * mm]});
            skFitSpline(sketch, "E236", {"points": [v(-267.27, 166.43) * mm, v(-266.84, 166.5) * mm, v(-265.73, 164.1) * mm, v(-264.96, 162.93) * mm]});
            skFitSpline(sketch, "E237", {"points": [v(-264.96, 162.93) * mm, v(-264.95, 162.9) * mm, v(-264.95, 162.87) * mm, v(-264.94, 162.84) * mm]});
            skFitSpline(sketch, "E238", {"points": [v(-266, 162.84) * mm, v(-266.58, 163.57) * mm, v(-267.9, 162.99) * mm, v(-267.34, 164.45) * mm]});
            skFitSpline(sketch, "E239", {"points": [v(-267.34, 164.45) * mm, v(-267.52, 165.85) * mm, v(-267.47, 166.4) * mm, v(-267.27, 166.43) * mm]});
            skFitSpline(sketch, "E240", {"points": [v(-358.09, 165.5) * mm, v(-356.72, 165.5) * mm, v(-355.68, 164.4) * mm, v(-356.75, 163.27) * mm]});
            skFitSpline(sketch, "E241", {"points": [v(-356.75, 163.27) * mm, v(-357.11, 163.22) * mm, v(-357.36, 163.06) * mm, v(-357.5, 162.84) * mm]});
            skFitSpline(sketch, "E242", {"points": [v(-358.06, 162.84) * mm, v(-358.1, 162.91) * mm, v(-358.17, 162.99) * mm, v(-358.23, 163.06) * mm]});
            skFitSpline(sketch, "E243", {"points": [v(-358.23, 163.06) * mm, v(-359.48, 163.15) * mm, v(-359.01, 164.3) * mm, v(-359.07, 165.32) * mm]});
            skFitSpline(sketch, "E244", {"points": [v(-359.07, 165.32) * mm, v(-358.74, 165.45) * mm, v(-358.4, 165.5) * mm, v(-358.09, 165.5) * mm]});
            skFitSpline(sketch, "E245", {"points": [v(-284.75, 165.05) * mm, v(-284.05, 165) * mm, v(-283.04, 164.04) * mm, v(-282.74, 163.37) * mm]});
            skFitSpline(sketch, "E246", {"points": [v(-282.74, 163.37) * mm, v(-282.64, 163.2) * mm, v(-282.54, 163.03) * mm, v(-282.44, 162.84) * mm]});
            skFitSpline(sketch, "E247", {"points": [v(-284.08, 162.84) * mm, v(-284.63, 163.54) * mm, v(-286.02, 163) * mm, v(-285.43, 164.45) * mm]});
            skFitSpline(sketch, "E248", {"points": [v(-285.43, 164.45) * mm, v(-285.33, 164.91) * mm, v(-285.08, 165.08) * mm, v(-284.75, 165.05) * mm]});
            skFitSpline(sketch, "E249", {"points": [v(-238.72, 165.05) * mm, v(-238, 165) * mm, v(-237, 164.04) * mm, v(-236.7, 163.37) * mm]});
            skFitSpline(sketch, "E250", {"points": [v(-236.7, 163.37) * mm, v(-236.6, 163.2) * mm, v(-236.5, 163.03) * mm, v(-236.4, 162.84) * mm]});
            skFitSpline(sketch, "E251", {"points": [v(-238.04, 162.84) * mm, v(-238.59, 163.54) * mm, v(-239.98, 163) * mm, v(-239.4, 164.45) * mm]});
            skFitSpline(sketch, "E252", {"points": [v(-239.4, 164.45) * mm, v(-239.3, 164.91) * mm, v(-239.04, 165.08) * mm, v(-238.72, 165.05) * mm]});
            skFitSpline(sketch, "E253", {"points": [v(-349.21, 164.1) * mm, v(-347.97, 164.08) * mm, v(-346.24, 163.8) * mm, v(-347.3, 163.24) * mm]});
            skFitSpline(sketch, "E254", {"points": [v(-347.3, 163.24) * mm, v(-347.59, 163.17) * mm, v(-347.79, 163.02) * mm, v(-347.92, 162.84) * mm]});
            skFitSpline(sketch, "E255", {"points": [v(-349.37, 162.84) * mm, v(-349.4, 162.88) * mm, v(-349.4, 162.9) * mm, v(-349.43, 162.94) * mm]});
            skFitSpline(sketch, "E256", {"points": [v(-349.43, 162.94) * mm, v(-349.85, 163.46) * mm, v(-350.95, 163.02) * mm, v(-350.17, 164.01) * mm]});
            skFitSpline(sketch, "E257", {"points": [v(-350.17, 164.01) * mm, v(-349.99, 164.07) * mm, v(-349.63, 164.1) * mm, v(-349.21, 164.1) * mm]});
            skSolve(sketch);
        }
        {
            var Q0;
            Q0 = qSketchRegion(id + "F0", true);
            extrude(context, id + "F1", {"entities" : qUnion([Q0]), "depth" : 3.8 * mm, "offsetDistance" : 25.4 * mm});
        }
    });
